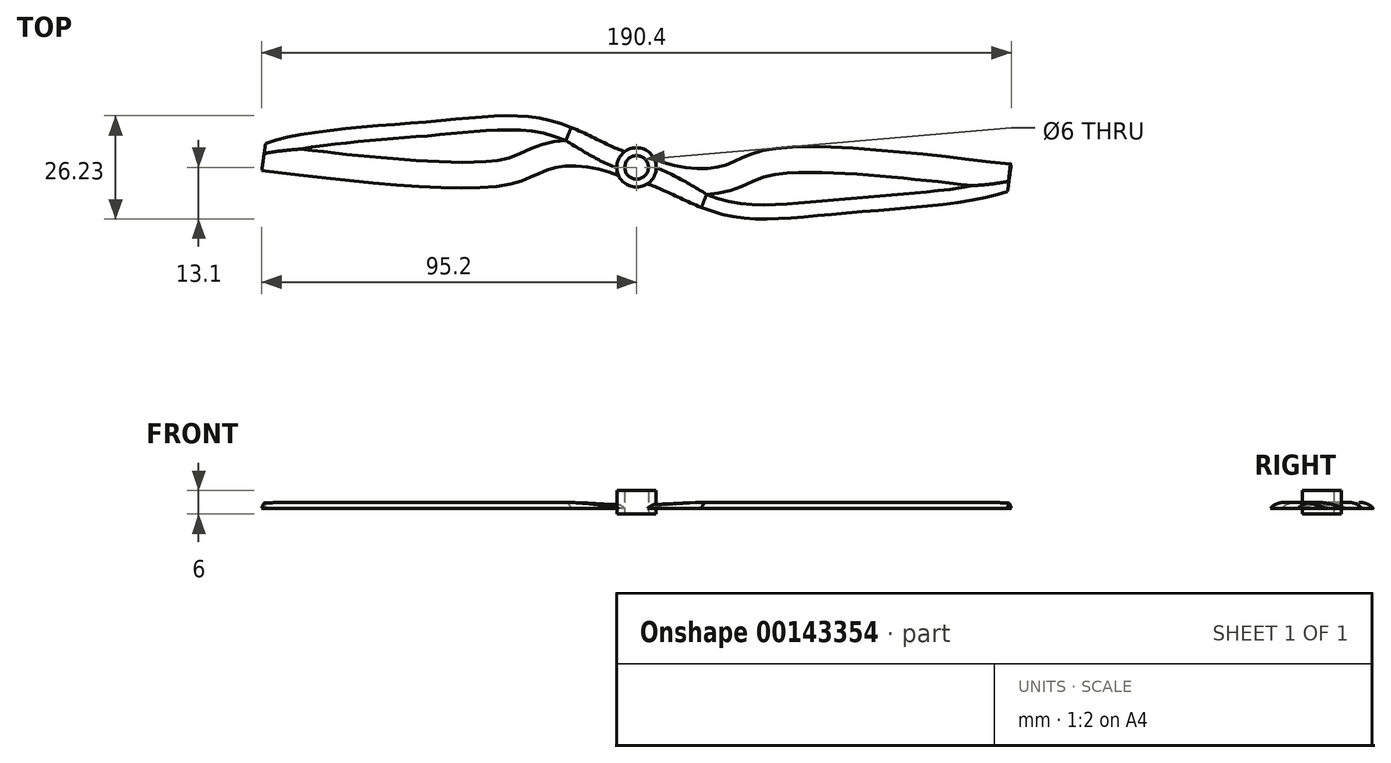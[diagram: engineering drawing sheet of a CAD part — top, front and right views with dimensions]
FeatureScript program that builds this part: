
annotation { "Feature Type Name" : "Feature", "Feature Type Description" : "" }
export const myFeature = defineFeature(function(context is Context, id is Id, definition is map)
    precondition{}
    {
        {
            var Q0;
            Q0=qCreatedBy(makeId("Top.planeOp"),FACE);
            var sketch = newSketch(context, id + "F0", { "sketchPlane" : qUnion([Q0])});
            skCircle(sketch, "E0", {"center": v(0, 0) * mm, "radius": 5 * mm});
            skCircle(sketch, "E1", {"center": v(0, 0) * mm, "radius": 3 * mm});
            skFitSpline(sketch, "E2", {"points": [v(-2.96, 4.03) * mm, v(-21.32, 11.8) * mm, v(-51.06, 11.8) * mm, v(-94.26, 6.1) * mm], "startDerivative": vector(-51.08, 15.58) * mm, "endDerivative": vector(-70.31, -25.59) * mm});
            skFitSpline(sketch, "E3", {"points": [v(-4.56, -2.06) * mm, v(-20.38, 0) * mm, v(-33.22, -4.49) * mm, v(-95.2, -0.8) * mm], "startDerivative": vector(-50.64, 23.12) * mm, "endDerivative": vector(-111.74, 12.85) * mm});
            skLineSegment(sketch, "E4", {"start": v(-94.26, 6.1) * mm, "end": v(-95.2, -0.8) * mm});
            skLineSegment(sketch, "E5.MirrorCS", {"start": v(94.98, 0.82) * mm, "end": v(95.2, -0.8) * mm});
            skFitSpline(sketch, "E6.MirrorCS", {"points": [v(2.76, -4.17) * mm, v(21.32, -11.8) * mm, v(51.06, -11.8) * mm, v(94.26, -6.1) * mm], "startDerivative": vector(51.08, -15.58) * mm, "endDerivative": vector(70.31, 25.59) * mm});
            skFitSpline(sketch, "E7.MirrorCS", {"points": [v(4.5, 2.16) * mm, v(20.38, 0) * mm, v(33.22, 4.49) * mm, v(95.2, 0.8) * mm], "startDerivative": vector(50.64, -23.12) * mm, "endDerivative": vector(111.74, -12.85) * mm});
            skPoint(sketch, "E8.MirrorCS.end.orphan", {"position": v(94.26, 6.1) * mm});
            skPoint(sketch, "E8.MirrorCS.start.orphan", {"position": v(2.96, 4.03) * mm});
            skLineSegment(sketch, "E9", {"start": v(95.2, 0.8) * mm, "end": v(94.26, -6.1) * mm});
            skSolve(sketch);
        }
        {
            var Q0;
            Q0=makeQuery(id+"F0.imprint","IMPRINT",FACE,{"disambiguationData":[TD([[makeQuery(id+"F0.imprint","IMPRINT",EDGE,{"derivedFrom":sQuery(id+"F0.wireOp",EDGE,"E1")}),-1.0]])]});
            extrude(context, id + "F1", {"entities" : qUnion([Q0]), "depth" : 3 * mm, "hasSecondDirection" : true, "secondDirectionOppositeDirection" : true, "secondDirectionDepth" : 3 * mm});
        }
        {
            var Q0;
            Q0 = qSketchRegion(id + "F0", true);
            extrude(context, id + "F2", {"entities" : qUnion([Q0]), "operationType" : NewBodyOperationType.ADD, "oppositeDirection" : true, "depth" : 1.5 * mm});
        }
        {
            var Q0;
            Q0=qCreatedBy(makeId("Top.planeOp"),FACE);
            cPlane(context, id + "F3", {"entities" : qUnion([Q0]), "cplaneType" : CPlaneType.OFFSET, "offset" : 25 * mm, "width" : 150 * mm, "height" : 150 * mm});
        }
        {
            var Q0;
            {var subQ0=sQuery(id+"F0.wireOp",EDGE,"E3");Q0=makeQuery(id+"F2.opExtrude","CAP_EDGE",EDGE,{"disambiguationData":[OSD([subQ0]),TDD([makeQuery(id+"F0.imprint","IMPRINT",EDGE,{"disambiguationData":[TD([[makeQuery(id+"F0.imprint","INTERSECT",VERTEX,{"derivedFrom":[subQ0,sQuery(id+"F0.wireOp",EDGE,"E4")]}),1.0]])],"derivedFrom":subQ0})])],"isStart":true});}
            var Q1;
            Q1=makeQuery(id+"F2.opExtrude","CAP_EDGE",EDGE,{"disambiguationData":[OSD([sQuery(id+"F0.wireOp",EDGE,"VZ5UIbRY-O6CE-YAD8-onvI-8Rn5FBbYOLpm")])],"isStart":true});
            var Q2;
            {var subQ0=sQuery(id+"F0.wireOp",EDGE,"E3");Q2=makeQuery(id+"F2.opExtrude","CAP_EDGE",EDGE,{"disambiguationData":[OSD([subQ0]),TDD([makeQuery(id+"F0.imprint","IMPRINT",EDGE,{"disambiguationData":[TD([[makeQuery(id+"F0.imprint","INTERSECT",VERTEX,{"derivedFrom":[sQuery(id+"F0.wireOp",EDGE,"E0"),subQ0]}),-1.0]])],"derivedFrom":subQ0})])],"isStart":true});}
            var Q3;
            Q3=makeQuery(id+"F2.opExtrude","CAP_EDGE",EDGE,{"disambiguationData":[OSD([sQuery(id+"F0.wireOp",EDGE,"E7.MirrorCS")])],"isStart":true});
            fillet(context, id + "F4", {"entities" : qUnion([Q0, Q1, Q2, Q3]), "radius" : 15 * mm, "tangentPropagation" : true, "allowEdgeOverflow" : false});
        }
        {
            var Q0;
            Q0=makeQuery(id+"F2.opExtrude","CAP_EDGE",EDGE,{"disambiguationData":[OSD([sQuery(id+"F0.wireOp",EDGE,"E2")])],"isStart":true});
            var Q1;
            Q1=makeQuery(id+"F2.opExtrude","CAP_EDGE",EDGE,{"disambiguationData":[OSD([sQuery(id+"F0.wireOp",EDGE,"E6.MirrorCS")])],"isStart":true});
            fillet(context, id + "F5", {"entities" : qUnion([Q0, Q1]), "radius" : 5 * mm, "tangentPropagation" : true, "allowEdgeOverflow" : false});
        }
    });
